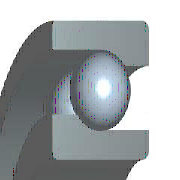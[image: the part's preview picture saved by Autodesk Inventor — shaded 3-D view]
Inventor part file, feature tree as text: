
AUTODESK INVENTOR PART (.ipt)
format: ipt  version: 2018 (Build 220112000, 112)  size: 304,640 bytes
history: native  units: mm (DEFAULTED — no unit token found)
features: other x5, plane x3, sketch x1, pattern_circular x1
ambient origin geometry x8: Origin, YZ Plane, XZ Plane, XY Plane, X Axis, Y Axis, Z Axis, Center Point
bodies: Solid1 (feature_tree)
feature tree (10):
  plane  "WorkPlane1"
  plane  "Work Plane2"
  plane  "WorkPlane2"
  other  "WorkPoint1"
  other  "WorkPoint3"
  other  "WorkPoint2"
  other  "WorkAxis1"
  sketch  "Schizzo7"
  other  "Work Axis2"
  pattern_circular  "Seriepolare1"  [2 undecoded]
note: 2 required parameter values undecoded (feature->parameter linkage not recoverable at this tier; creation-order binding heuristic only, values carry confidence <= 0.55)
